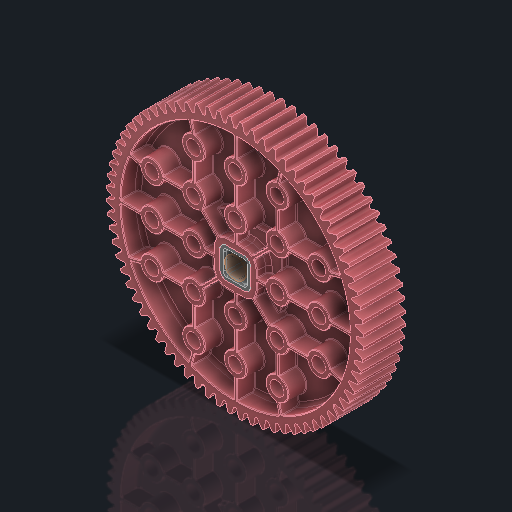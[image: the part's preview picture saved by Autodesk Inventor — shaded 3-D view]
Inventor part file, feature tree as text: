
AUTODESK INVENTOR PART (.ipt)
format: ipt  version: 2023.2 (Build 272271030, 271C)  size: 4,272,640 bytes
history: native  units: in
note: dims shown in document units (in); Inventor stores cm internally (conversion verified against a paired STEP export)
features: other x3, sketch x1, extrude x1
ambient origin geometry x8: Origin, YZ Plane, XZ Plane, XY Plane, X Axis, Y Axis, Z Axis, Center Point
bodies: Solid1 (feature_tree), Solid2 (feature_tree)
feature tree (5):
  sketch  "Sketch1"  dims[d0=0.25in d1=0.3937in d2=0.0in]
  other  "Srf1"
  other  "276-7574-001_OVERMOLD Rev4_72T 24DP Gear_1:1"
  other  "276-7573-002 Rev7_2:1"
  extrude  "ExtrusionSrf1"  Depth=0.3937in TaperAngle=0.0deg
